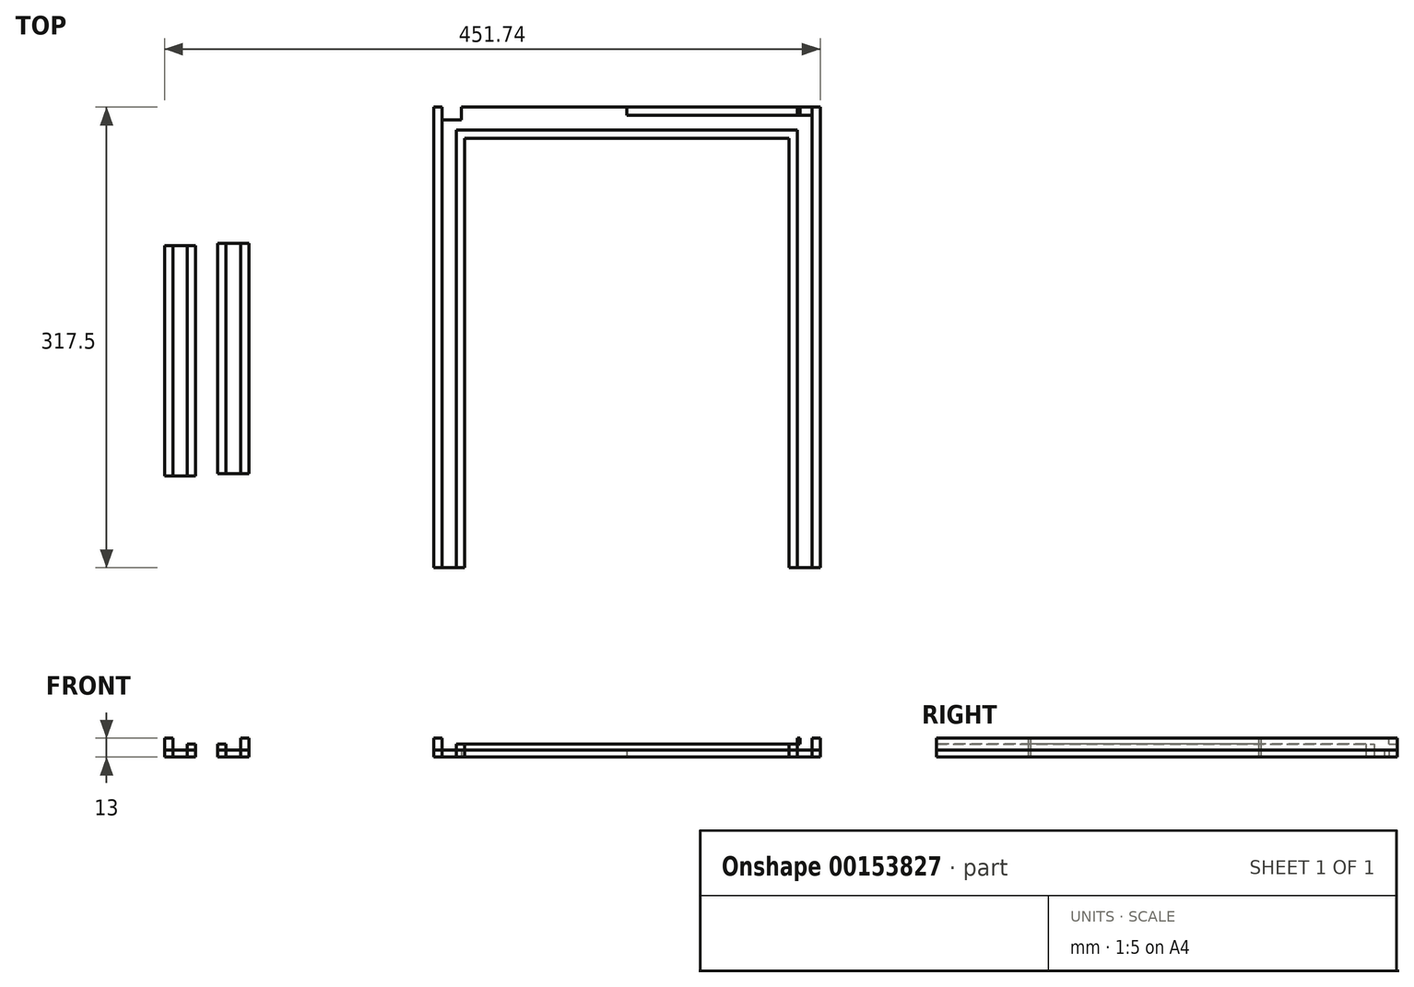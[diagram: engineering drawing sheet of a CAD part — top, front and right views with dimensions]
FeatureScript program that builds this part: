
annotation { "Feature Type Name" : "Feature", "Feature Type Description" : "" }
export const myFeature = defineFeature(function(context is Context, id is Id, definition is map)
    precondition{}
    {
        {
            var Q0;
            Q0=qCreatedBy(makeId("Top.planeOp"),FACE);
            var sketch = newSketch(context, id + "F0", { "sketchPlane" : qUnion([Q0])});
            skLineSegment(sketch, "E0.top", {"start": v(-195.38, -317.09) * mm, "end": v(-173.98, -317.09) * mm});
            skLineSegment(sketch, "E0.left", {"start": v(-195.38, -20.99) * mm, "end": v(-195.38, -317.09) * mm});
            skLineSegment(sketch, "E0.right", {"start": v(-173.98, -20.99) * mm, "end": v(-173.98, -317.09) * mm});
            skLineSegment(sketch, "E1.bottom", {"start": v(-195.38, 0.41) * mm, "end": v(-62.24, 0.41) * mm});
            skLineSegment(sketch, "E1.top", {"start": v(-173.98, -20.99) * mm, "end": v(-62.24, -20.99) * mm});
            skLineSegment(sketch, "E1.left", {"start": v(-195.38, 0.41) * mm, "end": v(-195.38, -20.99) * mm});
            skLineSegment(sketch, "E1.right", {"start": v(-62.24, 0.41) * mm, "end": v(-62.24, -20.99) * mm});
            skLineSegment(sketch, "E2.bottom", {"start": v(-189.68, -5.29) * mm, "end": v(-62.24, -5.29) * mm});
            skLineSegment(sketch, "E2.top", {"start": v(-179.68, -15.29) * mm, "end": v(-62.24, -15.29) * mm});
            skLineSegment(sketch, "E2.left", {"start": v(-189.68, -5.29) * mm, "end": v(-189.68, -15.29) * mm});
            skLineSegment(sketch, "E2.right", {"start": v(-62.24, -5.29) * mm, "end": v(-62.24, -15.29) * mm});
            skLineSegment(sketch, "E3.top", {"start": v(-189.68, -317.09) * mm, "end": v(-179.68, -317.09) * mm});
            skLineSegment(sketch, "E3.left", {"start": v(-189.68, 0.41) * mm, "end": v(-189.68, -317.09) * mm});
            skLineSegment(sketch, "E3.right", {"start": v(-179.68, -15.29) * mm, "end": v(-179.68, -317.09) * mm});
            skLineSegment(sketch, "E4", {"start": v(-189.68, -15.29) * mm, "end": v(-189.68, 0.41) * mm});
            skLineSegment(sketch, "E5.bottom", {"start": v(-62.24, 0.41) * mm, "end": v(70.91, 0.41) * mm});
            skLineSegment(sketch, "E5.top", {"start": v(-62.24, -20.99) * mm, "end": v(49.51, -20.99) * mm});
            skLineSegment(sketch, "E5.right", {"start": v(70.91, 0.41) * mm, "end": v(70.91, -20.99) * mm});
            skLineSegment(sketch, "E6.bottom", {"start": v(-62.24, -5.29) * mm, "end": v(65.21, -5.29) * mm});
            skLineSegment(sketch, "E6.top", {"start": v(-62.24, -15.29) * mm, "end": v(55.21, -15.29) * mm});
            skLineSegment(sketch, "E6.right", {"start": v(70.91, 0.41) * mm, "end": v(70.91, -5.29) * mm});
            skLineSegment(sketch, "E7.top", {"start": v(49.51, -317.09) * mm, "end": v(70.91, -317.09) * mm});
            skLineSegment(sketch, "E7.left", {"start": v(49.51, -20.99) * mm, "end": v(49.51, -317.09) * mm});
            skLineSegment(sketch, "E7.right", {"start": v(70.91, -20.99) * mm, "end": v(70.91, -317.09) * mm});
            skLineSegment(sketch, "E8.top", {"start": v(55.21, -317.09) * mm, "end": v(65.21, -317.09) * mm});
            skLineSegment(sketch, "E8.left", {"start": v(55.21, -15.29) * mm, "end": v(55.21, -317.09) * mm});
            skLineSegment(sketch, "E8.right", {"start": v(65.21, -5.29) * mm, "end": v(65.21, -317.09) * mm});
            skLineSegment(sketch, "E9", {"start": v(55.21, -15.29) * mm, "end": v(55.21, -15.29) * mm});
            skLineSegment(sketch, "E10", {"start": v(65.21, -5.29) * mm, "end": v(65.21, -5.29) * mm});
            skSolve(sketch);
        }
        {
            var Q0;
            {var subQ2=sQuery(id+"F0.wireOp",EDGE,"E0.left");Q0=makeQuery(id+"F0.imprint","IMPRINT",FACE,{"disambiguationData":[TD([[makeQuery(id+"F0.imprint","IMPRINT",EDGE,{"derivedFrom":subQ2}),1.0]])]});}
            var Q1;
            {var subQ3=sQuery(id+"F0.wireOp",EDGE,"E5.bottom");Q1=makeQuery(id+"F0.imprint","IMPRINT",FACE,{"disambiguationData":[TD([[makeQuery(id+"F0.imprint","IMPRINT",EDGE,{"derivedFrom":subQ3}),-1.0]])]});}
            var Q2;
            {var subQ1=sQuery(id+"F0.wireOp",EDGE,"E0.right");Q2=makeQuery(id+"F0.imprint","IMPRINT",FACE,{"disambiguationData":[TD([[makeQuery(id+"F0.imprint","IMPRINT",EDGE,{"derivedFrom":subQ1}),-1.0]])]});}
            var Q3;
            {var subQ2=sQuery(id+"F0.wireOp",EDGE,"E5.top");Q3=makeQuery(id+"F0.imprint","IMPRINT",FACE,{"disambiguationData":[TD([[makeQuery(id+"F0.imprint","IMPRINT",EDGE,{"derivedFrom":subQ2}),1.0]])]});}
            extrude(context, id + "F1", {"entities" : qUnion([Q0, Q1, Q2, Q3]), "depth" : 13 * mm});
        }
        {
            var Q0;
            Q0 = qSketchRegion(id + "F0", true);
            extrude(context, id + "F2", {"entities" : qUnion([Q0]), "depth" : 5 * mm});
        }
        {
            var Q0;
            Q0=qCreatedBy(makeId("Top.planeOp"),FACE);
            var sketch = newSketch(context, id + "F3", { "sketchPlane" : qUnion([Q0])});
            skLineSegment(sketch, "E11.bottom", {"start": v(-380.83, -95.04) * mm, "end": v(-359.43, -95.04) * mm});
            skLineSegment(sketch, "E11.top", {"start": v(-380.83, -253.79) * mm, "end": v(-359.43, -253.79) * mm});
            skLineSegment(sketch, "E11.left", {"start": v(-380.83, -95.04) * mm, "end": v(-380.83, -253.79) * mm});
            skLineSegment(sketch, "E11.right", {"start": v(-359.43, -95.04) * mm, "end": v(-359.43, -253.79) * mm});
            skLineSegment(sketch, "E12.bottom", {"start": v(-375.13, -95.04) * mm, "end": v(-365.13, -95.04) * mm});
            skLineSegment(sketch, "E12.top", {"start": v(-375.13, -253.79) * mm, "end": v(-365.13, -253.79) * mm});
            skLineSegment(sketch, "E12.left", {"start": v(-375.13, -95.04) * mm, "end": v(-375.13, -253.79) * mm});
            skLineSegment(sketch, "E12.right", {"start": v(-365.13, -95.04) * mm, "end": v(-365.13, -253.79) * mm});
            skLineSegment(sketch, "E13.bottom", {"start": v(-344.23, -93.51) * mm, "end": v(-322.83, -93.51) * mm});
            skLineSegment(sketch, "E13.top", {"start": v(-344.23, -252.26) * mm, "end": v(-322.83, -252.26) * mm});
            skLineSegment(sketch, "E13.left", {"start": v(-344.23, -93.51) * mm, "end": v(-344.23, -252.26) * mm});
            skLineSegment(sketch, "E13.right", {"start": v(-322.83, -93.51) * mm, "end": v(-322.83, -252.26) * mm});
            skLineSegment(sketch, "E14.bottom", {"start": v(-338.53, -93.51) * mm, "end": v(-328.53, -93.51) * mm});
            skLineSegment(sketch, "E14.top", {"start": v(-338.53, -252.26) * mm, "end": v(-328.53, -252.26) * mm});
            skLineSegment(sketch, "E14.left", {"start": v(-338.53, -93.51) * mm, "end": v(-338.53, -252.26) * mm});
            skLineSegment(sketch, "E14.right", {"start": v(-328.53, -93.51) * mm, "end": v(-328.53, -252.26) * mm});
            skSolve(sketch);
        }
        {
            var Q0;
            {var subQ0=sQuery(id+"F3.wireOp",EDGE,"E11.left");Q0=makeQuery(id+"F3.imprint","IMPRINT",FACE,{"disambiguationData":[TD([[makeQuery(id+"F3.imprint","IMPRINT",EDGE,{"derivedFrom":subQ0}),1.0]])]});}
            var Q1;
            {var subQ0=sQuery(id+"F3.wireOp",EDGE,"E13.right");Q1=makeQuery(id+"F3.imprint","IMPRINT",FACE,{"disambiguationData":[TD([[makeQuery(id+"F3.imprint","IMPRINT",EDGE,{"derivedFrom":subQ0}),-1.0]])]});}
            extrude(context, id + "F4", {"entities" : qUnion([Q0, Q1]), "depth" : 13 * mm});
        }
        {
            var Q0;
            Q0 = qSketchRegion(id + "F3", true);
            extrude(context, id + "F5", {"entities" : qUnion([Q0]), "depth" : 5 * mm});
        }
        {
            var Q0;
            Q0=qCreatedBy(makeId("Front.planeOp"),FACE);
            var sketch = newSketch(context, id + "F6", { "sketchPlane" : qUnion([Q0])});
            skLineSegment(sketch, "E15", {"start": v(-179.68, 0) * mm, "end": v(-173.98, 0) * mm, "construction": true});
            skLineSegment(sketch, "E16", {"start": v(-173.98, 0) * mm, "end": v(-173.98, 5) * mm, "construction": true});
            skLineSegment(sketch, "E17", {"start": v(-173.98, 5) * mm, "end": v(-173.98, 9) * mm, "construction": true});
            skLineSegment(sketch, "E18", {"start": v(-173.98, 9) * mm, "end": v(-179.68, 9) * mm, "construction": true});
            skLineSegment(sketch, "E19", {"start": v(-179.68, 9) * mm, "end": v(-179.68, 5) * mm, "construction": true});
            skLineSegment(sketch, "E20", {"start": v(-179.68, 5) * mm, "end": v(-179.68, 0) * mm, "construction": true});
            skLineSegment(sketch, "E21", {"start": v(-179.68, 5) * mm, "end": v(-173.98, 5) * mm, "construction": true});
            skLineSegment(sketch, "E22", {"start": v(-176.83, 0) * mm, "end": v(-176.83, 13) * mm, "construction": true});
            skLineSegment(sketch, "E23", {"start": v(49.51, 0) * mm, "end": v(55.21, 0) * mm, "construction": true});
            skLineSegment(sketch, "E24", {"start": v(55.21, 0) * mm, "end": v(55.21, 5) * mm, "construction": true});
            skLineSegment(sketch, "E25", {"start": v(55.21, 5) * mm, "end": v(55.21, 9) * mm, "construction": true});
            skLineSegment(sketch, "E26", {"start": v(55.21, 9) * mm, "end": v(49.51, 9) * mm, "construction": true});
            skLineSegment(sketch, "E27", {"start": v(49.51, 9) * mm, "end": v(49.51, 5) * mm, "construction": true});
            skLineSegment(sketch, "E28", {"start": v(49.51, 5) * mm, "end": v(49.51, 0) * mm, "construction": true});
            skLineSegment(sketch, "E29", {"start": v(49.51, 5) * mm, "end": v(55.21, 5) * mm, "construction": true});
            skLineSegment(sketch, "E30", {"start": v(52.36, 0) * mm, "end": v(52.36, 13) * mm, "construction": true});
            skLineSegment(sketch, "E31.bottom", {"start": v(-179.68, 9) * mm, "end": v(55.21, 9) * mm});
            skLineSegment(sketch, "E31.top", {"start": v(-179.68, 13) * mm, "end": v(55.21, 13) * mm});
            skLineSegment(sketch, "E31.left", {"start": v(-179.68, 9) * mm, "end": v(-179.68, 13) * mm});
            skLineSegment(sketch, "E31.right", {"start": v(55.21, 9) * mm, "end": v(55.21, 13) * mm});
            skSolve(sketch);
        }
        {
            var Q0;
            Q0 = qSketchRegion(id + "F6", true);
            extrude(context, id + "F7", {"entities" : qUnion([Q0]), "operationType" : NewBodyOperationType.REMOVE, "endBound" : BoundingType.SYMMETRIC, "depth" : 642.62 * mm});
        }
        {
            var Q0;
            Q0=qCreatedBy(makeId("Front.planeOp"),FACE);
            var sketch = newSketch(context, id + "F8", { "sketchPlane" : qUnion([Q0])});
            skLineSegment(sketch, "E32", {"start": v(57.1, 9) * mm, "end": v(70.91, 9) * mm, "construction": true});
            skLineSegment(sketch, "E33", {"start": v(65.21, 13) * mm, "end": v(65.21, 5) * mm, "construction": true});
            skLineSegment(sketch, "E34.bottom", {"start": v(65.21, 13) * mm, "end": v(57.1, 13) * mm});
            skLineSegment(sketch, "E34.top", {"start": v(65.21, 9) * mm, "end": v(57.1, 9) * mm});
            skLineSegment(sketch, "E34.left", {"start": v(65.21, 13) * mm, "end": v(65.21, 9) * mm});
            skLineSegment(sketch, "E34.right", {"start": v(57.1, 13) * mm, "end": v(57.1, 9) * mm});
            skSolve(sketch);
        }
        {
            var Q0;
            Q0 = qSketchRegion(id + "F8", true);
            extrude(context, id + "F9", {"entities" : qUnion([Q0]), "operationType" : NewBodyOperationType.REMOVE, "endBound" : BoundingType.SYMMETRIC, "oppositeDirection" : true, "depth" : 500 * mm});
        }
        {
            var Q0;
            Q0=qCreatedBy(makeId("Front.planeOp"),FACE);
            var sketch = newSketch(context, id + "F10", { "sketchPlane" : qUnion([Q0])});
            skLineSegment(sketch, "E35", {"start": v(-62.24, 5) * mm, "end": v(70.91, 5) * mm, "construction": true});
            skLineSegment(sketch, "E36", {"start": v(65.21, 9) * mm, "end": v(65.21, 5) * mm, "construction": true});
            skLineSegment(sketch, "E37.bottom", {"start": v(65.21, 9) * mm, "end": v(-62.24, 9) * mm});
            skLineSegment(sketch, "E37.top", {"start": v(65.21, 5) * mm, "end": v(-62.24, 5) * mm});
            skLineSegment(sketch, "E37.left", {"start": v(65.21, 9) * mm, "end": v(65.21, 5) * mm});
            skLineSegment(sketch, "E37.right", {"start": v(-62.24, 9) * mm, "end": v(-62.24, 5) * mm});
            skSolve(sketch);
        }
        {
            var Q0;
            Q0 = qSketchRegion(id + "F10", true);
            extrude(context, id + "F11", {"entities" : qUnion([Q0]), "operationType" : NewBodyOperationType.REMOVE, "endBound" : BoundingType.SYMMETRIC, "depth" : 12 * mm});
        }
        {
            var Q0;
            Q0=qCreatedBy(makeId("Top.planeOp"),FACE);
            var sketch = newSketch(context, id + "F12", { "sketchPlane" : qUnion([Q0])});
            skLineSegment(sketch, "E38.bottom", {"start": v(-69.8, -8.39) * mm, "end": v(184.2, -8.39) * mm});
            skLineSegment(sketch, "E38.top", {"start": v(-69.8, -325.89) * mm, "end": v(184.2, -325.89) * mm});
            skLineSegment(sketch, "E38.left", {"start": v(-69.8, -8.39) * mm, "end": v(-69.8, -325.89) * mm});
            skLineSegment(sketch, "E38.right", {"start": v(184.2, -8.39) * mm, "end": v(184.2, -325.89) * mm});
            skSolve(sketch);
        }
        {
            var Q0;
            {var subQ0=sQuery(id+"F3.wireOp",EDGE,"E11.right");Q0=makeQuery(id+"F3.imprint","IMPRINT",FACE,{"disambiguationData":[TD([[makeQuery(id+"F3.imprint","IMPRINT",EDGE,{"derivedFrom":subQ0}),-1.0]])]});}
            var Q1;
            {var subQ0=sQuery(id+"F3.wireOp",EDGE,"E13.left");Q1=makeQuery(id+"F3.imprint","IMPRINT",FACE,{"disambiguationData":[TD([[makeQuery(id+"F3.imprint","IMPRINT",EDGE,{"derivedFrom":subQ0}),1.0]])]});}
            extrude(context, id + "F13", {"entities" : qUnion([Q0, Q1]), "depth" : 9 * mm});
        }
        {
            var Q0;
            Q0=qCreatedBy(makeId("Top.planeOp"),FACE);
            var sketch = newSketch(context, id + "F14", { "sketchPlane" : qUnion([Q0])});
            skLineSegment(sketch, "E39", {"start": v(-189.68, 0.41) * mm, "end": v(-176.18, 0.41) * mm});
            skLineSegment(sketch, "E40", {"start": v(-176.18, 0.41) * mm, "end": v(-176.18, -8.39) * mm});
            skLineSegment(sketch, "E41", {"start": v(-176.18, -8.39) * mm, "end": v(-189.68, -8.39) * mm});
            skLineSegment(sketch, "E42", {"start": v(-189.68, -8.39) * mm, "end": v(-189.68, 0.41) * mm});
            skSolve(sketch);
        }
        {
            var Q0;
            Q0 = qSketchRegion(id + "F14", true);
            extrude(context, id + "F15", {"entities" : qUnion([Q0]), "operationType" : NewBodyOperationType.REMOVE, "depth" : 25 * mm});
        }
    });
